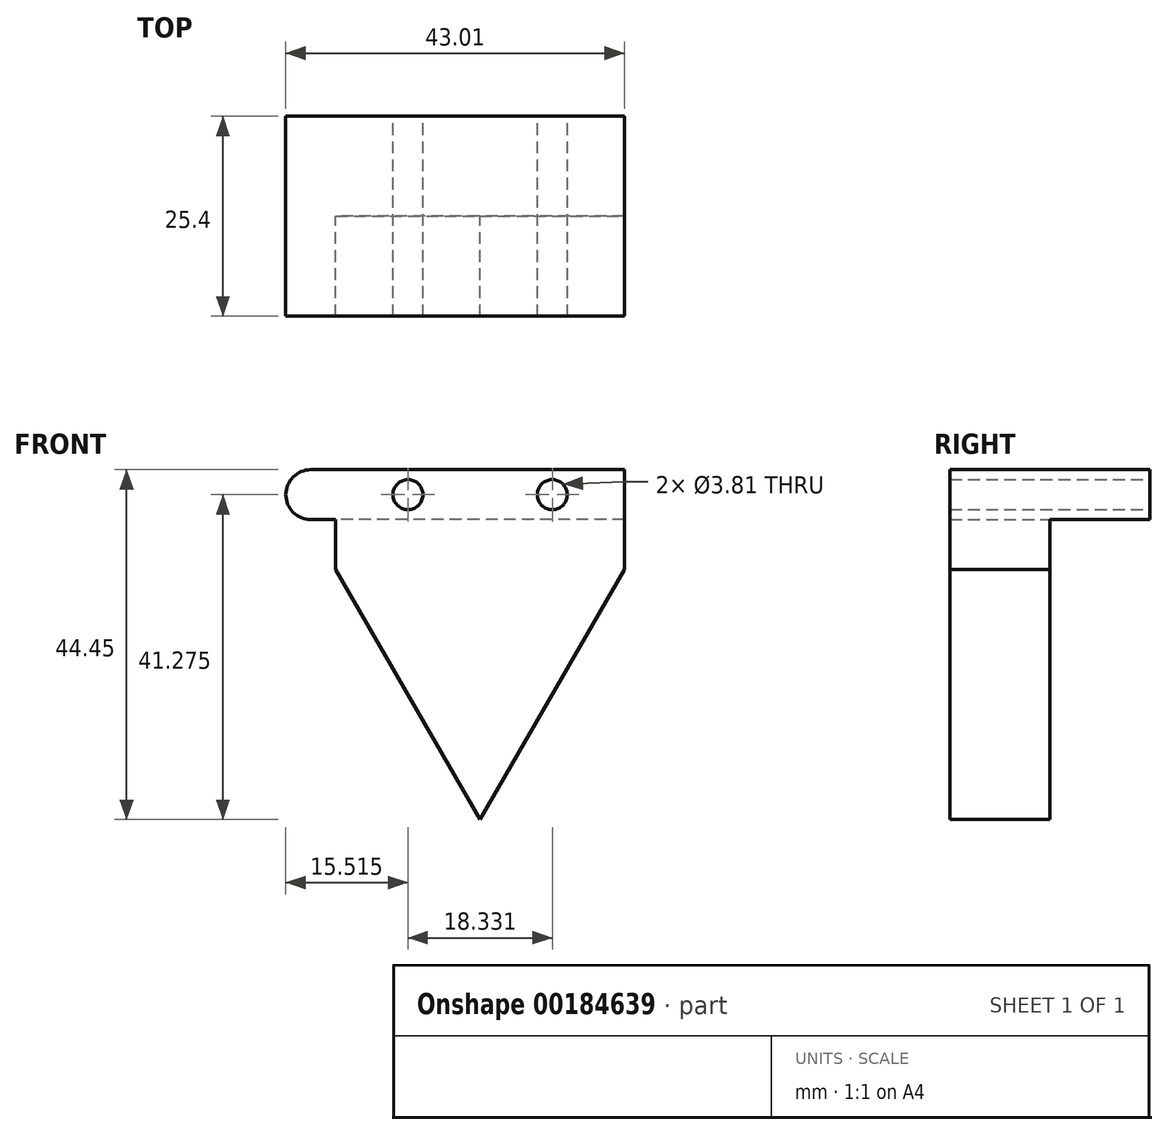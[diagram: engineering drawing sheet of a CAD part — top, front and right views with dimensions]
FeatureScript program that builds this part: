
annotation { "Feature Type Name" : "Feature", "Feature Type Description" : "" }
export const myFeature = defineFeature(function(context is Context, id is Id, definition is map)
    precondition{}
    {
        {
            var Q0;
            Q0=qCreatedBy(makeId("Front.planeOp"),FACE);
            var sketch = newSketch(context, id + "F0", { "sketchPlane" : qUnion([Q0])});
            skLineSegment(sketch, "E0", {"start": v(32.97, -15.18) * mm, "end": v(32.97, -2.48) * mm});
            skLineSegment(sketch, "E1", {"start": v(-3.69, -15.18) * mm, "end": v(-3.69, -2.48) * mm});
            skLineSegment(sketch, "E2", {"start": v(-3.69, -2.48) * mm, "end": v(32.97, -2.48) * mm});
            skPoint(sketch, "E3", {"position": v(-3.69, -8.83) * mm});
            skLineSegment(sketch, "E4", {"start": v(32.97, -8.83) * mm, "end": v(-3.69, -8.83) * mm});
            skLineSegment(sketch, "E5", {"start": v(-3.69, -2.48) * mm, "end": v(-6.86, -2.48) * mm});
            skLineSegment(sketch, "E6", {"start": v(-3.69, -8.83) * mm, "end": v(-6.86, -8.83) * mm});
            skPoint(sketch, "E7", {"position": v(-6.86, -5.65) * mm});
            skCircle(sketch, "E8", {"center": v(-6.86, -5.65) * mm, "radius": 3.18 * mm});
            skLineSegment(sketch, "E9", {"start": v(-3.69, -8.83) * mm, "end": v(-3.69, -2.48) * mm});
            skLineSegment(sketch, "E10", {"start": v(32.97, -8.83) * mm, "end": v(32.97, -2.48) * mm});
            skLineSegment(sketch, "E11", {"start": v(-3.69, -15.18) * mm, "end": v(14.64, -46.93) * mm});
            skLineSegment(sketch, "E12", {"start": v(14.64, -46.93) * mm, "end": v(32.97, -15.18) * mm});
            skPoint(sketch, "E13", {"position": v(5.48, -5.65) * mm});
            skPoint(sketch, "E14", {"position": v(23.8, -5.65) * mm});
            skCircle(sketch, "E15", {"center": v(5.48, -5.65) * mm, "radius": 1.9 * mm});
            skCircle(sketch, "E16", {"center": v(23.8, -5.65) * mm, "radius": 1.9 * mm});
            skCircle(sketch, "E17", {"center": v(-6.86, -5.65) * mm, "radius": 1.9 * mm});
            skSolve(sketch);
        }
        {
            var Q0;
            {var subQ1=sQuery(id+"F0.wireOp",EDGE,"E2");Q0=makeQuery(id+"F0.imprint","IMPRINT",FACE,{"disambiguationData":[TD([[makeQuery(id+"F0.imprint","IMPRINT",EDGE,{"derivedFrom":subQ1}),-1.0]])]});}
            var Q1;
            Q1=makeQuery(id+"F0.imprint","IMPRINT",FACE,{"disambiguationData":[TD([[makeQuery(id+"F0.imprint","IMPRINT",EDGE,{"derivedFrom":sQuery(id+"F0.wireOp",EDGE,"E0")}),1.0]])]});
            var Q2;
            Q2=makeQuery(id+"F0.imprint","IMPRINT",FACE,{"disambiguationData":[TD([[makeQuery(id+"F0.imprint","IMPRINT",EDGE,{"derivedFrom":sQuery(id+"F0.wireOp",EDGE,"E17")}),-1.0]])]});
            var Q3;
            {var subQ0=sQuery(id+"F0.wireOp",EDGE,"E5");Q3=makeQuery(id+"F0.imprint","IMPRINT",FACE,{"disambiguationData":[TD([[makeQuery(id+"F0.imprint","IMPRINT",EDGE,{"derivedFrom":subQ0}),1.0]])]});}
            var Q4;
            {var subQ0=sQuery(id+"F0.wireOp",EDGE,"E6");Q4=makeQuery(id+"F0.imprint","IMPRINT",FACE,{"disambiguationData":[TD([[makeQuery(id+"F0.imprint","IMPRINT",EDGE,{"derivedFrom":subQ0}),-1.0]])]});}
            var Q5;
            Q5=makeQuery(id+"F0.imprint","IMPRINT",FACE,{"disambiguationData":[TD([[makeQuery(id+"F0.imprint","IMPRINT",EDGE,{"derivedFrom":sQuery(id+"F0.wireOp",EDGE,"E17")}),1.0]])]});
            extrude(context, id + "F1", {"entities" : qUnion([Q0, Q1, Q2, Q3, Q4, Q5]), "depth" : 12.7 * mm});
        }
        {
            var Q0;
            {var subQ1=sQuery(id+"F0.wireOp",EDGE,"E2");Q0=makeQuery(id+"F0.imprint","IMPRINT",FACE,{"disambiguationData":[TD([[makeQuery(id+"F0.imprint","IMPRINT",EDGE,{"derivedFrom":subQ1}),-1.0]])]});}
            var Q1;
            Q1=makeQuery(id+"F0.imprint","IMPRINT",FACE,{"disambiguationData":[TD([[makeQuery(id+"F0.imprint","IMPRINT",EDGE,{"derivedFrom":sQuery(id+"F0.wireOp",EDGE,"E17")}),-1.0]])]});
            var Q2;
            {var subQ0=sQuery(id+"F0.wireOp",EDGE,"E5");Q2=makeQuery(id+"F0.imprint","IMPRINT",FACE,{"disambiguationData":[TD([[makeQuery(id+"F0.imprint","IMPRINT",EDGE,{"derivedFrom":subQ0}),1.0]])]});}
            var Q3;
            {var subQ0=sQuery(id+"F0.wireOp",EDGE,"E6");Q3=makeQuery(id+"F0.imprint","IMPRINT",FACE,{"disambiguationData":[TD([[makeQuery(id+"F0.imprint","IMPRINT",EDGE,{"derivedFrom":subQ0}),-1.0]])]});}
            extrude(context, id + "F2", {"entities" : qUnion([Q0, Q1, Q2, Q3]), "operationType" : NewBodyOperationType.ADD, "oppositeDirection" : true, "depth" : 12.7 * mm});
        }
        {
            var Q0;
            Q0=makeQuery(id+"F0.imprint","IMPRINT",FACE,{"disambiguationData":[TD([[makeQuery(id+"F0.imprint","IMPRINT",EDGE,{"derivedFrom":sQuery(id+"F0.wireOp",EDGE,"E17")}),1.0]])]});
            extrude(context, id + "F3", {"entities" : qUnion([Q0]), "operationType" : NewBodyOperationType.ADD, "oppositeDirection" : true, "depth" : 12.7 * mm});
        }
    });
